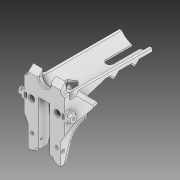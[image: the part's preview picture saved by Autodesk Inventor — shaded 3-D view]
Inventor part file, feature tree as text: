
AUTODESK INVENTOR PART (.ipt)
format: ipt  version: 2020 (Build 240168000, 168)  size: 550,400 bytes
history: native  units: in
note: dims shown in document units (in); Inventor stores cm internally (conversion verified against a paired STEP export)
features: extrude x11, sketch x11, projected_geometry x3, plane x1, mirror x1, imported_body x1
ambient origin geometry x8: Origin, YZ Plane, XZ Plane, XY Plane, X Axis, Y Axis, Z Axis, Center Point
bodies: Solid1 (feature_tree)
feature tree (28):
  extrude  "Extrusion1"  Depth=0.315in
  extrude  "Extrusion2"  Depth=0.2756in TaperAngle=0.0deg
  extrude  "Extrusion9"  Depth=0.3937in TaperAngle=0.0deg
  extrude  "Extrusion10"  Depth=0.1181in TaperAngle=0.0deg
  plane  "Work Plane1"
  extrude  "Extrusion11"  Depth=0.0787in
  mirror  "Mirror1"
  extrude  "Extrusion3"  Depth=0.3937in TaperAngle=0.0deg
  extrude  "Extrusion7"  Depth=0.0787in
  extrude  "Extrusion4"  Depth=0.1378in
  extrude  "Extrusion5"  Depth=0.0787in
  extrude  "Extrusion6"  Depth=0.2165in
  extrude  "Extrusion8"  Depth=0.1024in TaperAngle=0.0deg
  sketch  "Sketch1"  dims[d0=0.3937in d1=0.0in d2=0.315in]
  sketch  "Sketch2"  dims[d3=0.1378in d4=0.2756in d5=0.0in]
  sketch  "Sketch3"  dims[d6=0.3937in d7=0.0in d8=0.3937in d9=0.0in]
  projected_geometry  "Projected Loop1"
  sketch  "Sketch4"  dims[d10=0.1181in d11=0.0in d12=0.1181in d13=0.0in]
  sketch  "Sketch5"  dims[d14=1.5866in d15=0.0787in]
  projected_geometry  "Projected Loop2"
  sketch  "Sketch6"  dims[d16=0.3937in d17=0.1181in d18=0.0in]
  projected_geometry  "Projected Loop3"
  sketch  "Sketch7"  dims[d19=0.0in d20=0.0in d21=0.0787in]
  sketch  "Sketch8"  dims[d22=0.1181in d23=0.0in d24=0.1378in]
  sketch  "Sketch9"  dims[d25=0.4724in d26=0.0in d27=0.0787in]
  sketch  "Sketch10"  dims[d28=0.2165in d29=0.2165in]
  sketch  "Sketch11"  dims[d30=0.1969in d31=0.1024in d32=0.0in]
  imported_body  "Base1"
